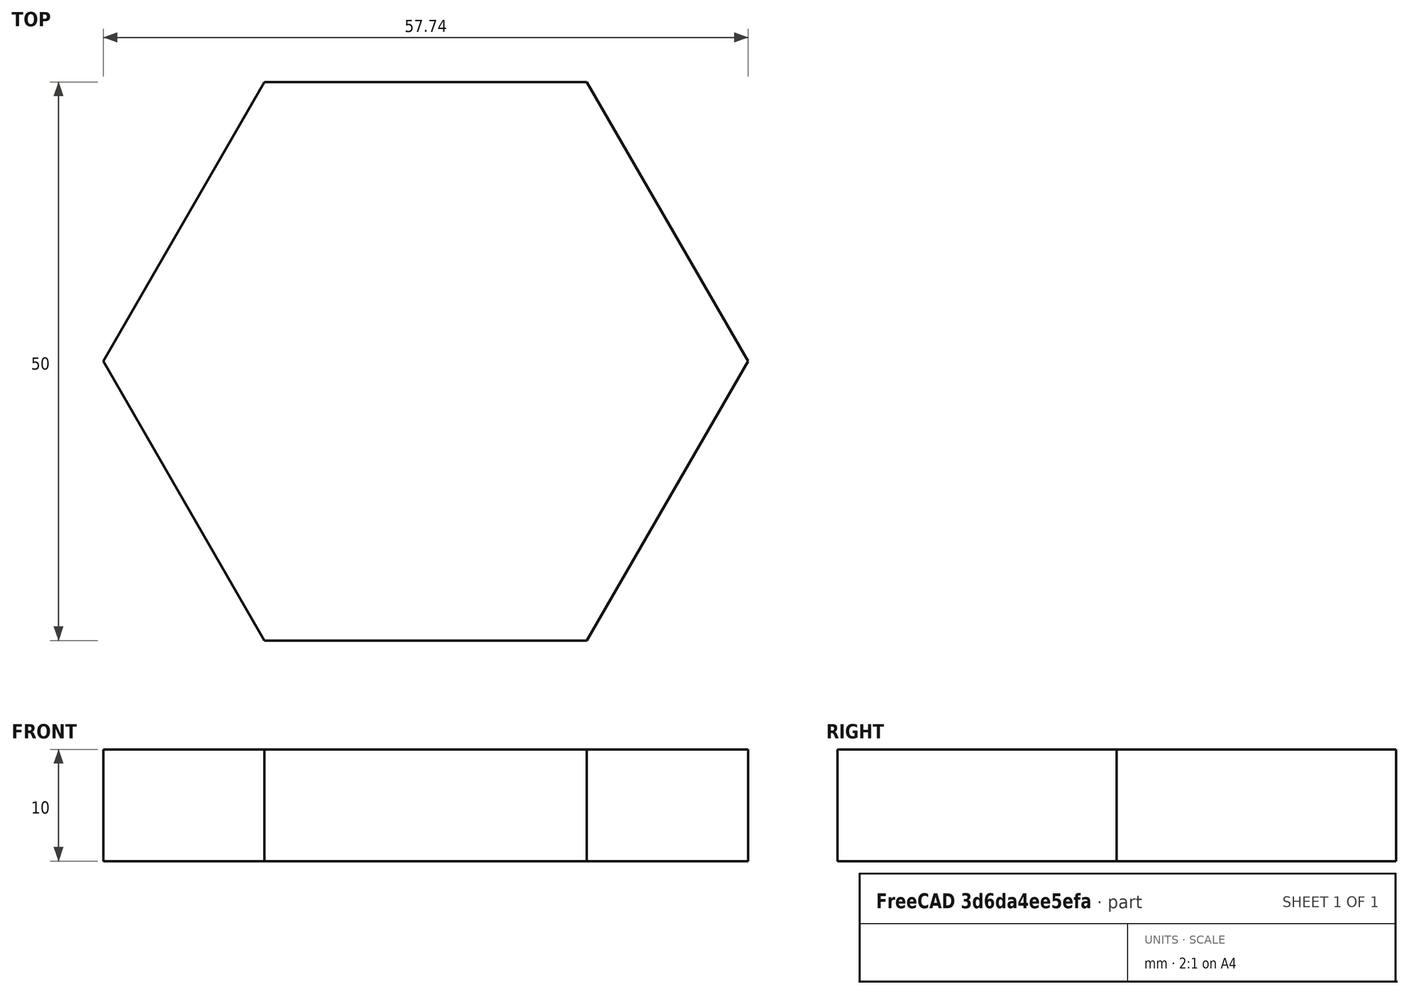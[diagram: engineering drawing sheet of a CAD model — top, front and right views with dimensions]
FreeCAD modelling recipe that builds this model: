
FCSTD DOCUMENT  (FreeCAD 1.0R39109 (Git))
Label: simplepoly
License: All rights reserved
LicenseURL: https://en.wikipedia.org/wiki/All_rights_reserved
objects: Sketcher::SketchObject×1, Part::Extrusion×1
note: 3 computed .brp shape members not serialized (recipe doc carries the construction recipe); baked Part::Feature solids carry a one-line shape summary decoded from their .brp

FEATURE [Sketcher::SketchObject] Sketch
  ArcFitTolerance = 1e-06
  FullyConstrained = true
  MakeInternals = false
  sketch-geometry (7):
    g0: LineSegment StartX=28.8675 StartY=0 StartZ=0 EndX=14.4338 EndY=25 EndZ=0
    g1: LineSegment StartX=14.4338 StartY=25 StartZ=0 EndX=-14.4338 EndY=25 EndZ=0
    g2: LineSegment StartX=-14.4338 StartY=25 StartZ=0 EndX=-28.8675 EndY=-8.88e-14 EndZ=0
    g3: LineSegment StartX=-28.8675 StartY=-8.88e-14 StartZ=0 EndX=-14.4338 EndY=-25 EndZ=0
    g4: LineSegment StartX=-14.4338 StartY=-25 StartZ=0 EndX=14.4338 EndY=-25 EndZ=0
    g5: LineSegment StartX=14.4338 StartY=-25 StartZ=0 EndX=28.8675 EndY=0 EndZ=0
    g6: Circle [constr] CenterX=0 CenterY=0 CenterZ=0 NormalX=0 NormalY=0 NormalZ=1 AngleXU=0 Radius=28.8675
  constraints (16):
    c: Coincident(g0,g1)
    c: Coincident(g1,g2)
    c: Coincident(g2,g3)
    c: Coincident(g3,g4)
    c: Coincident(g4,g5)
    c: Coincident(g5,g0)
    c: Equal(g0, g1-g5) x5
    c: PointOnObject(g0,g6)
    c: PointOnObject(g1,g6)
    c: PointOnObject(g2,g6)
    c: PointOnObject(g3,g6)
    c: PointOnObject(g4,g6)
    c: PointOnObject(g5,g6)
    c: Coincident(g6,g-1)
    c: PointOnObject(g5,g-1)
    c: Distance(g5,g2) = 50
FEATURE [Part::Extrusion] Extrude
  Base = -> Sketch
  Dir = (0,0,1)
  DirMode = 2
  FaceMakerClass = Part::FaceMakerBullseye
  FaceMakerMode = 3
  LengthFwd = 10
  LengthRev = 0
  Solid = true
  Symmetric = false
